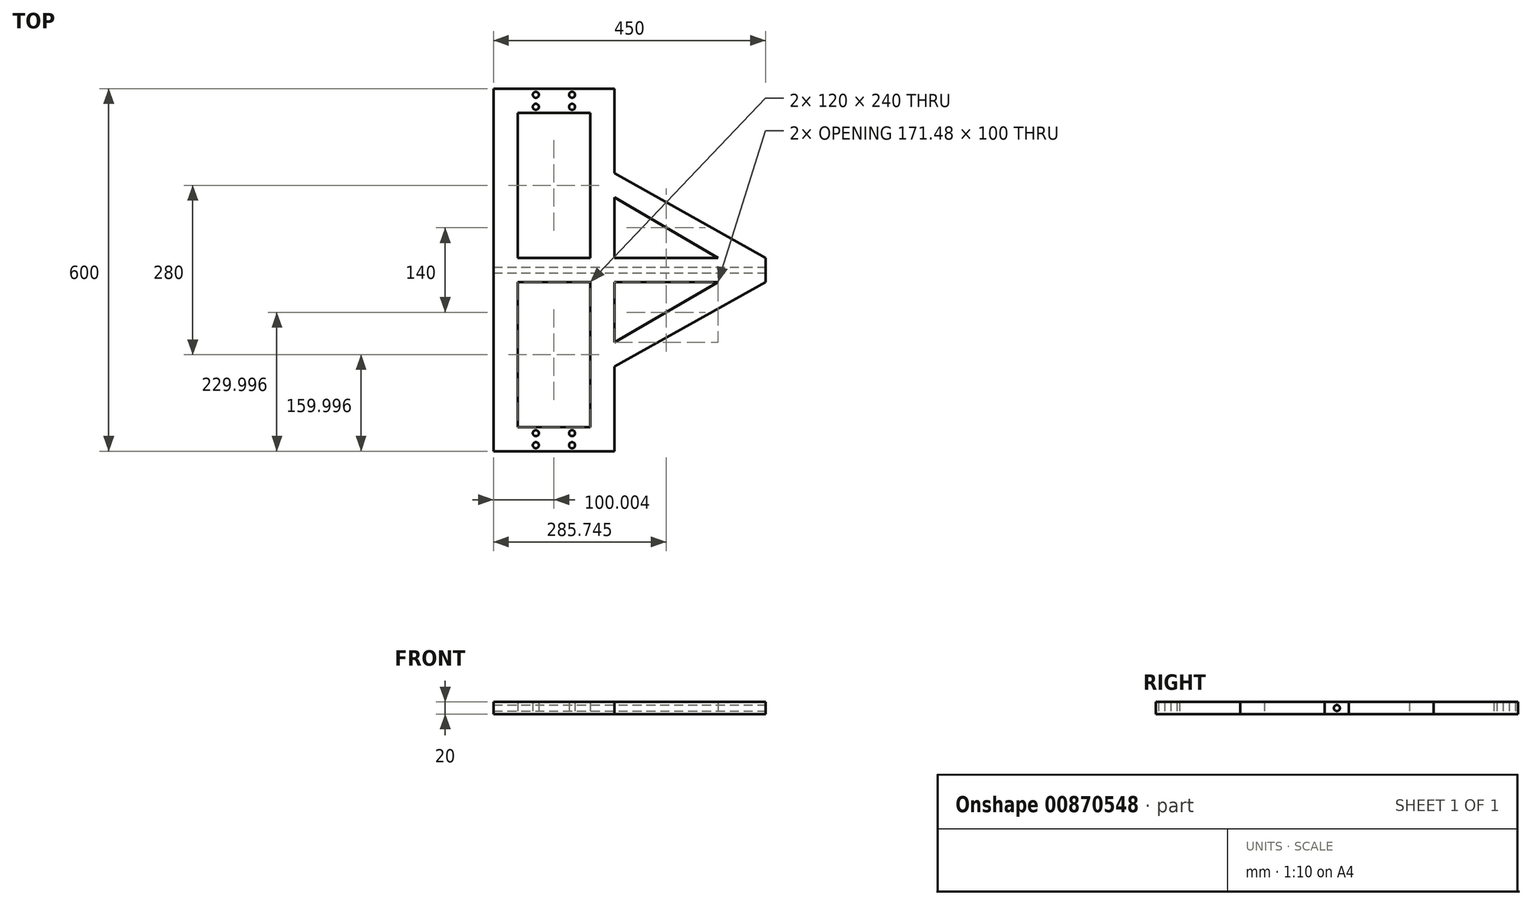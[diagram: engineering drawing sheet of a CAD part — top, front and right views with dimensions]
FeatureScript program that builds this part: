
annotation { "Feature Type Name" : "Feature", "Feature Type Description" : "" }
export const myFeature = defineFeature(function(context is Context, id is Id, definition is map)
    precondition{}
    {
        {
            var Q0;
            Q0=qCreatedBy(makeId("Top.planeOp"),FACE);
            var sketch = newSketch(context, id + "F0", { "sketchPlane" : qUnion([Q0])});
            skLineSegment(sketch, "E0.bottom", {"start": v(-559.53, 349.33) * mm, "end": v(-359.53, 349.33) * mm});
            skLineSegment(sketch, "E0.top", {"start": v(-559.53, -250.67) * mm, "end": v(-359.53, -250.67) * mm});
            skLineSegment(sketch, "E0.left", {"start": v(-559.53, 349.33) * mm, "end": v(-559.53, -250.67) * mm});
            skLineSegment(sketch, "E0.right", {"start": v(-359.53, 349.33) * mm, "end": v(-359.53, -250.67) * mm});
            skLineSegment(sketch, "E1.bottom", {"start": v(-519.53, 309.33) * mm, "end": v(-399.53, 309.33) * mm});
            skLineSegment(sketch, "E1.top", {"start": v(-519.53, -210.67) * mm, "end": v(-399.53, -210.67) * mm});
            skLineSegment(sketch, "E1.left", {"start": v(-519.53, 309.33) * mm, "end": v(-519.53, -210.67) * mm});
            skLineSegment(sketch, "E1.right", {"start": v(-399.53, 309.33) * mm, "end": v(-399.53, -210.67) * mm});
            skPoint(sketch, "E2", {"position": v(-489.53, 339.33) * mm});
            skPoint(sketch, "E3", {"position": v(-489.53, 319.33) * mm});
            skPoint(sketch, "E4", {"position": v(-429.53, 319.33) * mm});
            skPoint(sketch, "E5", {"position": v(-489.53, -220.67) * mm});
            skPoint(sketch, "E6", {"position": v(-489.53, -240.67) * mm});
            skPoint(sketch, "E7", {"position": v(-429.53, -240.67) * mm});
            skPoint(sketch, "E8", {"position": v(-429.53, -220.67) * mm});
            skLineSegment(sketch, "E9", {"start": v(-519.53, 29.33) * mm, "end": v(-399.53, 29.33) * mm});
            skLineSegment(sketch, "E10", {"start": v(-519.53, 69.33) * mm, "end": v(-399.53, 69.33) * mm});
            skPoint(sketch, "E11", {"position": v(-459.53, 49.33) * mm});
            skPoint(sketch, "E12", {"position": v(-429.53, 339.33) * mm});
            skLineSegment(sketch, "E13", {"start": v(-399.53, 29.33) * mm, "end": v(-109.53, 29.33) * mm});
            skLineSegment(sketch, "E14", {"start": v(-399.53, 69.33) * mm, "end": v(-109.53, 69.33) * mm});
            skLineSegment(sketch, "E15", {"start": v(-109.53, 29.33) * mm, "end": v(-109.53, 69.33) * mm});
            skLineSegment(sketch, "E16", {"start": v(-109.53, 29.33) * mm, "end": v(-359.53, -110.67) * mm});
            skLineSegment(sketch, "E17", {"start": v(-109.53, 69.33) * mm, "end": v(-359.53, 209.33) * mm});
            skLineSegment(sketch, "E18", {"start": v(-359.53, -70.67) * mm, "end": v(-188.04, 29.33) * mm});
            skLineSegment(sketch, "E19", {"start": v(-188.04, 69.33) * mm, "end": v(-359.53, 169.33) * mm});
            skSolve(sketch);
        }
        {
            var Q0;
            Q0=makeQuery(id+"F0.imprint","IMPRINT",FACE,{"disambiguationData":[TD([[makeQuery(id+"F0.imprint","IMPRINT",EDGE,{"derivedFrom":sQuery(id+"F0.wireOp",EDGE,"E0.bottom")}),-1.0]])]});
            extrude(context, id + "F1", {"entities" : qUnion([Q0]), "depth" : 20 * mm, "offsetDistance" : 25 * mm});
        }
        {
            var Q0;
            Q0=sQuery(id+"F0.wireOp",VERTEX,"E2");
            var Q1;
            Q1=sQuery(id+"F0.wireOp",VERTEX,"85043d42-c259-4e1b-9cff-e973773782c9");
            var Q2;
            Q2=sQuery(id+"F0.wireOp",VERTEX,"E4");
            var Q3;
            Q3=sQuery(id+"F0.wireOp",VERTEX,"E3");
            var Q4;
            Q4=sQuery(id+"F0.wireOp",VERTEX,"E5");
            var Q5;
            Q5=sQuery(id+"F0.wireOp",VERTEX,"E6");
            var Q6;
            Q6=sQuery(id+"F0.wireOp",VERTEX,"E7");
            var Q7;
            Q7=sQuery(id+"F0.wireOp",VERTEX,"E8");
            var Q8;
            Q8=makeQuery(id+"F1.opExtrude","SWEPT_BODY",BODY,{"disambiguationData":[OSD([sQuery(id+"F0.wireOp",EDGE,"E0.bottom"),sQuery(id+"F0.wireOp",EDGE,"E0.top"),sQuery(id+"F0.wireOp",EDGE,"E0.left"),sQuery(id+"F0.wireOp",EDGE,"E0.right"),sQuery(id+"F0.wireOp",EDGE,"E1.bottom"),sQuery(id+"F0.wireOp",EDGE,"E1.top"),sQuery(id+"F0.wireOp",EDGE,"E1.left"),sQuery(id+"F0.wireOp",EDGE,"E1.right")])]});
            hole(context, id + "F2", {"style" : HoleStyle.SIMPLE, "endStyle" : HoleEndStyle.THROUGH, "oppositeDirection" : true, "holeDiameter" : 10 * mm, "majorDiameter" : 5 * mm, "isTappedThrough" : true, "tappedDepth" : 12 * mm, "tapClearance" : 3, "locations" : qUnion([Q0, Q1, Q2, Q3, Q4, Q5, Q6, Q7]), "scope" : qUnion([Q8])});
        }
        {
            var Q0;
            Q0=sQuery(id+"F0.wireOp",VERTEX,"E12");
            var Q1;
            Q1=makeQuery(id+"F1.opExtrude","SWEPT_BODY",BODY,{"disambiguationData":[OSD([sQuery(id+"F0.wireOp",EDGE,"E0.bottom"),sQuery(id+"F0.wireOp",EDGE,"E0.top"),sQuery(id+"F0.wireOp",EDGE,"E0.left"),sQuery(id+"F0.wireOp",EDGE,"E0.right"),sQuery(id+"F0.wireOp",EDGE,"E1.bottom"),sQuery(id+"F0.wireOp",EDGE,"E1.top"),sQuery(id+"F0.wireOp",EDGE,"E1.left"),sQuery(id+"F0.wireOp",EDGE,"E1.right")])]});
            hole(context, id + "F3", {"style" : HoleStyle.SIMPLE, "endStyle" : HoleEndStyle.THROUGH, "oppositeDirection" : true, "holeDiameter" : 10 * mm, "majorDiameter" : 5 * mm, "isTappedThrough" : true, "tappedDepth" : 12 * mm, "tapClearance" : 3, "locations" : qUnion([Q0]), "scope" : qUnion([Q1])});
        }
        {
            var Q0;
            {var subQ0=sQuery(id+"F0.wireOp",EDGE,"E9");Q0=makeQuery(id+"F0.imprint","IMPRINT",FACE,{"disambiguationData":[TD([[makeQuery(id+"F0.imprint","IMPRINT",EDGE,{"derivedFrom":subQ0}),1.0]])]});}
            var Q1;
            {var subQ0=sQuery(id+"F0.wireOp",EDGE,"E14");var subQ1=sQuery(id+"F0.wireOp",EDGE,"E0.right");var subQ2=makeQuery(id+"F0.imprint","INTERSECT",VERTEX,{"derivedFrom":[subQ1,subQ0]});Q1=makeQuery(id+"F0.imprint","IMPRINT",FACE,{"disambiguationData":[TD([[makeQuery(id+"F0.imprint","IMPRINT",EDGE,{"disambiguationData":[TD([[subQ2,-1.0]])],"derivedFrom":subQ1}),-1.0]])]});}
            var Q2;
            {var subQ5=sQuery(id+"F0.wireOp",EDGE,"E15");Q2=makeQuery(id+"F0.imprint","IMPRINT",FACE,{"disambiguationData":[TD([[makeQuery(id+"F0.imprint","IMPRINT",EDGE,{"derivedFrom":subQ5}),1.0]])]});}
            var Q3;
            {var subQ0=sQuery(id+"F0.wireOp",EDGE,"hDTIDlhZ-GMzp-pDT5-Quoq-2bMvqdIp5SXq");Q3=makeQuery(id+"F0.imprint","IMPRINT",FACE,{"disambiguationData":[TD([[makeQuery(id+"F0.imprint","IMPRINT",EDGE,{"derivedFrom":subQ0}),1.0]])]});}
            var Q4;
            {var subQ0=sQuery(id+"F0.wireOp",EDGE,"5dFsTnay-xkD2-qJ7x-NzK9-uF85kCf1SLN5");Q4=makeQuery(id+"F0.imprint","IMPRINT",FACE,{"disambiguationData":[TD([[makeQuery(id+"F0.imprint","IMPRINT",EDGE,{"derivedFrom":subQ0}),1.0]])]});}
            var Q5;
            {var subQ0=sQuery(id+"F0.wireOp",EDGE,"jw8QNhgc-qR9E-Isiv-6YZF-UFKdUrX0E5to");Q5=makeQuery(id+"F0.imprint","IMPRINT",FACE,{"disambiguationData":[TD([[makeQuery(id+"F0.imprint","IMPRINT",EDGE,{"derivedFrom":subQ0}),1.0]])]});}
            var Q6;
            {var subQ0=sQuery(id+"F0.wireOp",EDGE,"E17");Q6=makeQuery(id+"F0.imprint","IMPRINT",FACE,{"disambiguationData":[TD([[makeQuery(id+"F0.imprint","IMPRINT",EDGE,{"derivedFrom":subQ0}),1.0]])]});}
            var Q7;
            {var subQ0=sQuery(id+"F0.wireOp",EDGE,"E16");Q7=makeQuery(id+"F0.imprint","IMPRINT",FACE,{"disambiguationData":[TD([[makeQuery(id+"F0.imprint","IMPRINT",EDGE,{"derivedFrom":subQ0}),-1.0]])]});}
            extrude(context, id + "F4", {"entities" : qUnion([Q0, Q1, Q2, Q3, Q4, Q5, Q6, Q7]), "operationType" : NewBodyOperationType.ADD, "depth" : 20 * mm, "offsetDistance" : 25 * mm});
        }
        {
            var Q0;
            Q0=makeQuery(id+"F4.opExtrude","SWEPT_FACE",FACE,{"disambiguationData":[OSD([sQuery(id+"F0.wireOp",EDGE,"E15")])]});
            var sketch = newSketch(context, id + "F5", { "sketchPlane" : qUnion([Q0])});
            skPoint(sketch, "E20", {"position": v(49.33, 10) * mm});
            skPoint(sketch, "E20.positionSnap0", {"position": v(49.33, 20) * mm});
            skSolve(sketch);
        }
        {
            var Q0;
            Q0=sQuery(id+"F5.wireOp",VERTEX,"E20");
            var Q1;
            Q1=makeQuery(id+"F1.opExtrude","SWEPT_BODY",BODY,{"disambiguationData":[OSD([sQuery(id+"F0.wireOp",EDGE,"E0.bottom"),sQuery(id+"F0.wireOp",EDGE,"E0.top"),sQuery(id+"F0.wireOp",EDGE,"E0.left"),sQuery(id+"F0.wireOp",EDGE,"E0.right"),sQuery(id+"F0.wireOp",EDGE,"E1.bottom"),sQuery(id+"F0.wireOp",EDGE,"E1.top"),sQuery(id+"F0.wireOp",EDGE,"E1.left"),sQuery(id+"F0.wireOp",EDGE,"E1.right"),sQuery(id+"F0.wireOp",EDGE,"E13"),sQuery(id+"F0.wireOp",EDGE,"E14")])]});
            hole(context, id + "F6", {"style" : HoleStyle.SIMPLE, "endStyle" : HoleEndStyle.THROUGH, "holeDiameter" : 10 * mm, "majorDiameter" : 5 * mm, "isTappedThrough" : true, "tappedDepth" : 12 * mm, "tapClearance" : 3, "locations" : qUnion([Q0]), "scope" : qUnion([Q1])});
        }
    });
